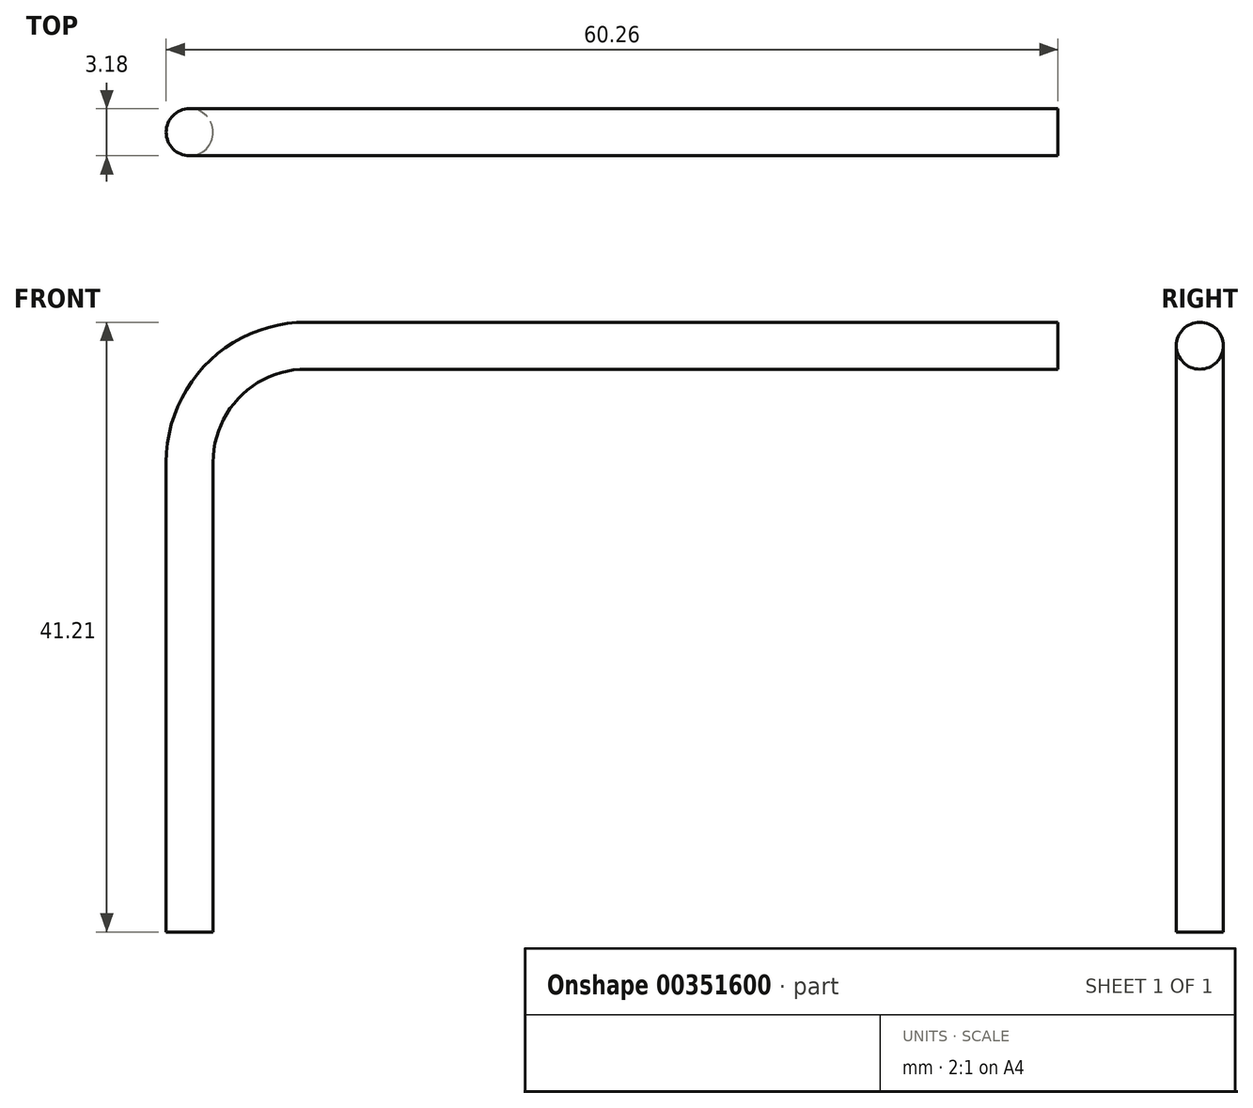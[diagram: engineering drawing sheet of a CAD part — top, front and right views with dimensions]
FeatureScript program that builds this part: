
annotation { "Feature Type Name" : "Feature", "Feature Type Description" : "" }
export const myFeature = defineFeature(function(context is Context, id is Id, definition is map)
    precondition{}
    {
        {
            var Q0;
            Q0=qCreatedBy(makeId("Front.planeOp"),FACE);
            var sketch = newSketch(context, id + "F0", { "sketchPlane" : qUnion([Q0])});
            skLineSegment(sketch, "E0", {"start": v(0, 0) * mm, "end": v(0, 31.75) * mm});
            skArc(sketch, "E1", {"start": v(7.87, 39.62) * mm, "mid": v(2.3, 37.32) * mm, "end": v(0, 31.75) * mm});
            skLineSegment(sketch, "E2", {"start": v(7.87, 39.62) * mm, "end": v(58.67, 39.62) * mm});
            skSolve(sketch);
        }
        {
            var Q0;
            Q0=qCreatedBy(makeId("Top.planeOp"),FACE);
            var sketch = newSketch(context, id + "F1", { "sketchPlane" : qUnion([Q0])});
            skCircle(sketch, "E3", {"center": v(0, 0) * mm, "radius": 1.59 * mm});
            skSolve(sketch);
        }
        {
            var Q0;
            Q0 = qSketchRegion(id + "F1", true);
            var Q1;
            Q1 = qConstructionFilter(qBodyType(qCreatedBy(id + "F0" ,EDGE), BodyType.WIRE), ConstructionObject.NO);
            sweep(context, id + "F2", {"profiles" : qUnion([Q0]), "path" : qUnion([Q1])});
        }
    });
